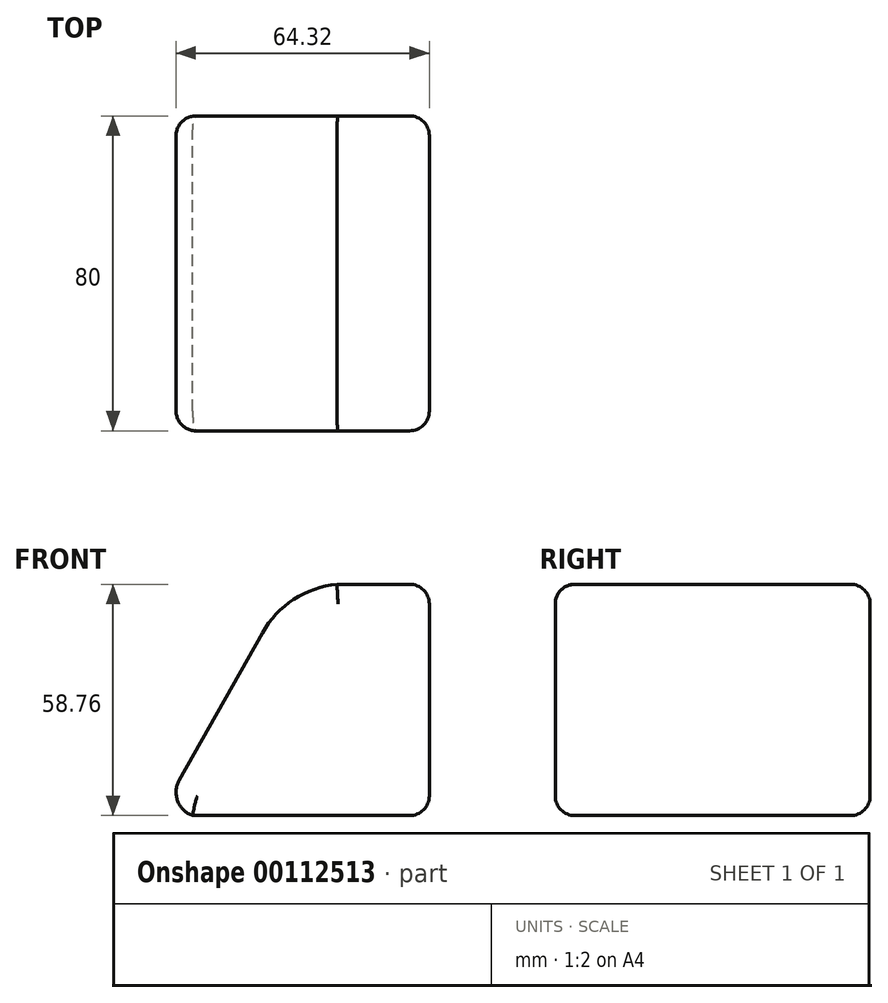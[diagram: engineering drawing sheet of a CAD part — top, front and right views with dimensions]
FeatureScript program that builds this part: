
annotation { "Feature Type Name" : "Feature", "Feature Type Description" : "" }
export const myFeature = defineFeature(function(context is Context, id is Id, definition is map)
    precondition{}
    {
        {
            var Q0;
            Q0=qCreatedBy(makeId("Front.planeOp"),FACE);
            var sketch = newSketch(context, id + "F0", { "sketchPlane" : qUnion([Q0])});
            skLineSegment(sketch, "E0", {"start": v(0, 5) * mm, "end": v(0, 53.76) * mm});
            skLineSegment(sketch, "E1", {"start": v(-5, 0) * mm, "end": v(-60.11, 0) * mm});
            skLineSegment(sketch, "E2", {"start": v(-5, 58.76) * mm, "end": v(-23.44, 58.76) * mm});
            skLineSegment(sketch, "E3", {"start": v(-63.51, 8.97) * mm, "end": v(-42.38, 46.44) * mm});
            skArc(sketch, "E4", {"start": v(-23.44, 58.76) * mm, "mid": v(-34.42, 54.92) * mm, "end": v(-42.38, 46.44) * mm});
            skArc(sketch, "E5", {"start": v(-63.51, 8.97) * mm, "mid": v(-63.91, 3.69) * mm, "end": v(-60.11, 0) * mm});
            skPoint(sketch, "E6.visualSharp", {"position": v(0, 0) * mm});
            skArc(sketch, "E6.filletArc", {"start": v(-5, 0) * mm, "mid": v(-1.46, 1.46) * mm, "end": v(0, 5) * mm});
            skPoint(sketch, "E7.visualSharp", {"position": v(0, 58.76) * mm});
            skArc(sketch, "E7.filletArc", {"start": v(0, 53.76) * mm, "mid": v(-1.46, 57.3) * mm, "end": v(-5, 58.76) * mm});
            skSolve(sketch);
        }
        {
            var Q0;
            Q0 = qSketchRegion(id + "F0", true);
            extrude(context, id + "F1", {"entities" : qUnion([Q0]), "depth" : 80 * mm});
        }
        {
            var Q0;
            Q0=makeQuery(id+"F1.opExtrude","CAP_EDGE",EDGE,{"disambiguationData":[OSD([sQuery(id+"F0.wireOp",EDGE,"E4")])],"isStart":false});
            var Q1;
            Q1=makeQuery(id+"F1.opExtrude","CAP_EDGE",EDGE,{"disambiguationData":[OSD([sQuery(id+"F0.wireOp",EDGE,"E2")])],"isStart":false});
            var Q2;
            Q2=makeQuery(id+"F1.opExtrude","CAP_EDGE",EDGE,{"disambiguationData":[OSD([sQuery(id+"F0.wireOp",EDGE,"E7.filletArc")])],"isStart":false});
            var Q3;
            Q3=makeQuery(id+"F1.opExtrude","CAP_EDGE",EDGE,{"disambiguationData":[OSD([sQuery(id+"F0.wireOp",EDGE,"E0")])],"isStart":false});
            var Q4;
            Q4=makeQuery(id+"F1.opExtrude","CAP_EDGE",EDGE,{"disambiguationData":[OSD([sQuery(id+"F0.wireOp",EDGE,"E6.filletArc")])],"isStart":false});
            var Q5;
            Q5=makeQuery(id+"F1.opExtrude","CAP_EDGE",EDGE,{"disambiguationData":[OSD([sQuery(id+"F0.wireOp",EDGE,"E1")])],"isStart":false});
            var Q6;
            Q6=makeQuery(id+"F1.opExtrude","CAP_EDGE",EDGE,{"disambiguationData":[OSD([sQuery(id+"F0.wireOp",EDGE,"E5")])],"isStart":false});
            var Q7;
            Q7=makeQuery(id+"F1.opExtrude","CAP_EDGE",EDGE,{"disambiguationData":[OSD([sQuery(id+"F0.wireOp",EDGE,"E3")])],"isStart":false});
            fillet(context, id + "F2", {"entities" : qUnion([Q0, Q1, Q2, Q3, Q4, Q5, Q6, Q7]), "radius" : 5 * mm, "tangentPropagation" : true, "allowEdgeOverflow" : false});
        }
        {
            var Q0;
            Q0=makeQuery(id+"F1.opExtrude","CAP_EDGE",EDGE,{"disambiguationData":[OSD([sQuery(id+"F0.wireOp",EDGE,"E2")])],"isStart":true});
            var Q1;
            Q1=makeQuery(id+"F1.opExtrude","CAP_EDGE",EDGE,{"disambiguationData":[OSD([sQuery(id+"F0.wireOp",EDGE,"E4")])],"isStart":true});
            var Q2;
            Q2=makeQuery(id+"F1.opExtrude","CAP_EDGE",EDGE,{"disambiguationData":[OSD([sQuery(id+"F0.wireOp",EDGE,"E3")])],"isStart":true});
            var Q3;
            Q3=makeQuery(id+"F1.opExtrude","CAP_EDGE",EDGE,{"disambiguationData":[OSD([sQuery(id+"F0.wireOp",EDGE,"E5")])],"isStart":true});
            var Q4;
            Q4=makeQuery(id+"F1.opExtrude","CAP_FACE",FACE,{"disambiguationData":[OSD([sQuery(id+"F0.wireOp",EDGE,"E0"),sQuery(id+"F0.wireOp",EDGE,"E1"),sQuery(id+"F0.wireOp",EDGE,"E2"),sQuery(id+"F0.wireOp",EDGE,"E3"),sQuery(id+"F0.wireOp",EDGE,"E4"),sQuery(id+"F0.wireOp",EDGE,"E5"),sQuery(id+"F0.wireOp",EDGE,"E6.filletArc"),sQuery(id+"F0.wireOp",EDGE,"E7.filletArc")])],"isStart":true});
            var Q5;
            Q5=makeQuery(id+"F1.opExtrude","CAP_EDGE",EDGE,{"disambiguationData":[OSD([sQuery(id+"F0.wireOp",EDGE,"E6.filletArc")])],"isStart":true});
            var Q6;
            Q6=makeQuery(id+"F1.opExtrude","CAP_EDGE",EDGE,{"disambiguationData":[OSD([sQuery(id+"F0.wireOp",EDGE,"E0")])],"isStart":true});
            fillet(context, id + "F3", {"entities" : qUnion([Q0, Q1, Q2, Q3, Q4, Q5, Q6]), "radius" : 5 * mm, "tangentPropagation" : true, "allowEdgeOverflow" : false});
        }
    });
